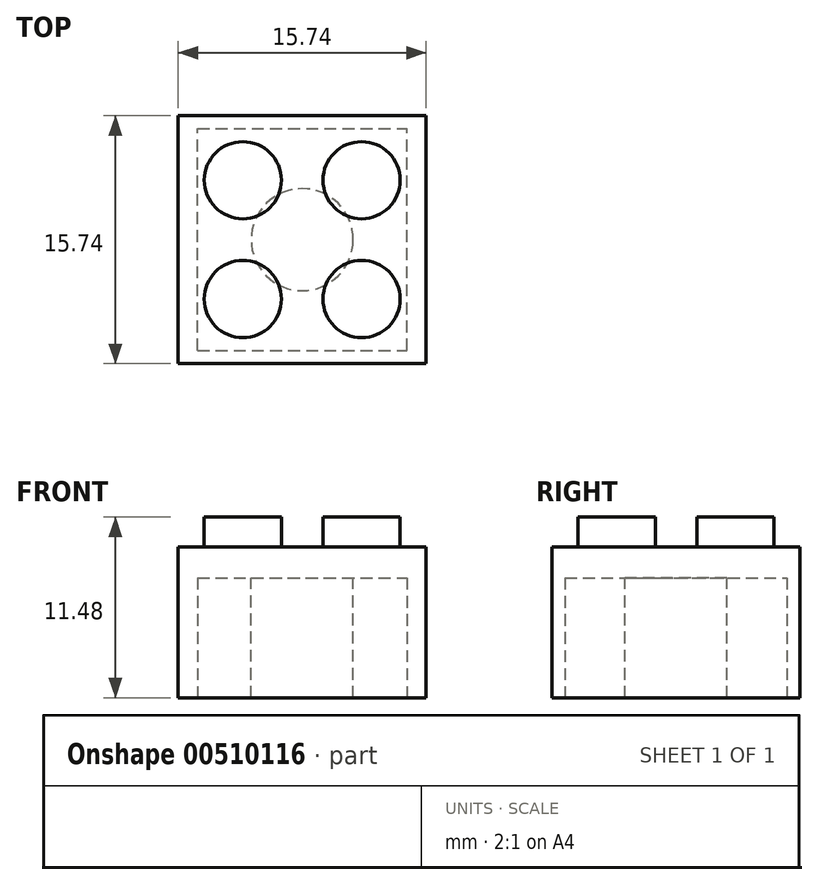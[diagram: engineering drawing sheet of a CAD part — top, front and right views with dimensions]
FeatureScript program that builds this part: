
annotation { "Feature Type Name" : "Feature", "Feature Type Description" : "" }
export const myFeature = defineFeature(function(context is Context, id is Id, definition is map)
    precondition{}
    {
        {
            var Q0;
            Q0=qCreatedBy(makeId("Top.planeOp"),FACE);
            var sketch = newSketch(context, id + "F0", { "sketchPlane" : qUnion([Q0])});
            skLineSegment(sketch, "E0.bottom", {"start": v(-7.87, 7.87) * mm, "end": v(7.87, 7.87) * mm});
            skLineSegment(sketch, "E0.top", {"start": v(-7.87, -7.87) * mm, "end": v(7.87, -7.87) * mm});
            skLineSegment(sketch, "E0.left", {"start": v(-7.87, 7.87) * mm, "end": v(-7.87, -7.87) * mm});
            skLineSegment(sketch, "E0.right", {"start": v(7.87, 7.87) * mm, "end": v(7.87, -7.87) * mm});
            skPoint(sketch, "E0.middle", {"position": v(0, 0) * mm});
            skSolve(sketch);
        }
        {
            var Q0;
            Q0=makeQuery(id+"F0.imprint","IMPRINT",FACE,{"disambiguationData":[TD([[makeQuery(id+"F0.imprint","IMPRINT",EDGE,{"derivedFrom":sQuery(id+"F0.wireOp",EDGE,"E0.bottom")}),-1.0]])]});
            extrude(context, id + "F1", {"entities" : qUnion([Q0]), "depth" : 9.58 * mm, "offsetDistance" : 25.4 * mm});
        }
        {
            var Q0;
            Q0=makeQuery(id+"F1.opExtrude","CAP_FACE",FACE,{"disambiguationData":[OSD([sQuery(id+"F0.wireOp",EDGE,"E0.bottom"),sQuery(id+"F0.wireOp",EDGE,"E0.top"),sQuery(id+"F0.wireOp",EDGE,"E0.left"),sQuery(id+"F0.wireOp",EDGE,"E0.right")])],"isStart":false});
            var sketch = newSketch(context, id + "F2", { "sketchPlane" : qUnion([Q0])});
            skCircle(sketch, "E1", {"center": v(-3.77, 3.77) * mm, "radius": 2.45 * mm});
            skSolve(sketch);
        }
        {
            var Q0;
            Q0=makeQuery(id+"F2.imprint","IMPRINT",FACE,{"disambiguationData":[TD([[makeQuery(id+"F2.imprint","IMPRINT",EDGE,{"derivedFrom":sQuery(id+"F2.wireOp",EDGE,"E1")}),-1.0]])]});
            var sketch = newSketch(context, id + "F3", { "sketchPlane" : qUnion([Q0])});
            skCircle(sketch, "E2", {"center": v(-3.77, -3.77) * mm, "radius": 2.45 * mm});
            skSolve(sketch);
        }
        {
            var Q0;
            Q0 = qSketchRegion(id + "F2", true);
            extrude(context, id + "F4", {"entities" : qUnion([Q0]), "operationType" : NewBodyOperationType.ADD, "depth" : 1.9 * mm, "offsetDistance" : 25.4 * mm});
        }
        {
            var Q0;
            Q0 = qSketchRegion(id + "F3", true);
            extrude(context, id + "F5", {"entities" : qUnion([Q0]), "operationType" : NewBodyOperationType.ADD, "depth" : 1.9 * mm, "offsetDistance" : 25.4 * mm});
        }
        {
            var Q0;
            Q0=makeQuery(id+"F1.opExtrude","CAP_FACE",FACE,{"disambiguationData":[OSD([sQuery(id+"F0.wireOp",EDGE,"E0.bottom"),sQuery(id+"F0.wireOp",EDGE,"E0.top"),sQuery(id+"F0.wireOp",EDGE,"E0.left"),sQuery(id+"F0.wireOp",EDGE,"E0.right")])],"isStart":false});
            var sketch = newSketch(context, id + "F6", { "sketchPlane" : qUnion([Q0])});
            skCircle(sketch, "E3", {"center": v(3.77, 3.77) * mm, "radius": 2.45 * mm});
            skCircle(sketch, "E4", {"center": v(3.77, -3.77) * mm, "radius": 2.45 * mm});
            skSolve(sketch);
        }
        {
            var Q0;
            Q0 = qSketchRegion(id + "F6", true);
            extrude(context, id + "F7", {"entities" : qUnion([Q0]), "operationType" : NewBodyOperationType.ADD, "depth" : 1.9 * mm, "offsetDistance" : 25.4 * mm});
        }
        {
            var Q0;
            Q0=makeQuery(id+"F1.opExtrude","CAP_FACE",FACE,{"disambiguationData":[OSD([sQuery(id+"F0.wireOp",EDGE,"E0.bottom"),sQuery(id+"F0.wireOp",EDGE,"E0.top"),sQuery(id+"F0.wireOp",EDGE,"E0.left"),sQuery(id+"F0.wireOp",EDGE,"E0.right")])],"isStart":true});
            var sketch = newSketch(context, id + "F8", { "sketchPlane" : qUnion([Q0])});
            skLineSegment(sketch, "E5.bottom", {"start": v(-6.64, 7.04) * mm, "end": v(6.64, 7.04) * mm});
            skLineSegment(sketch, "E5.top", {"start": v(-6.64, -7.04) * mm, "end": v(6.64, -7.04) * mm});
            skLineSegment(sketch, "E5.left", {"start": v(-6.64, 7.04) * mm, "end": v(-6.64, -7.04) * mm});
            skLineSegment(sketch, "E5.right", {"start": v(6.64, 7.04) * mm, "end": v(6.64, -7.04) * mm});
            skPoint(sketch, "E5.middle", {"position": v(0, 0) * mm});
            skSolve(sketch);
        }
        {
            var Q0;
            Q0=makeQuery(id+"F8.imprint","IMPRINT",FACE,{"disambiguationData":[TD([[makeQuery(id+"F8.imprint","IMPRINT",EDGE,{"derivedFrom":sQuery(id+"F8.wireOp",EDGE,"E5.bottom")}),-1.0]])]});
            extrude(context, id + "F9", {"entities" : qUnion([Q0]), "operationType" : NewBodyOperationType.REMOVE, "oppositeDirection" : true, "depth" : 7.62 * mm, "offsetDistance" : 25.4 * mm});
        }
        {
            var Q0;
            Q0=makeQuery(id+"F9.boolean.opBoolean","COPY",FACE,{"derivedFrom":makeQuery(id+"F9.opExtrude","CAP_FACE",FACE,{"disambiguationData":[OSD([sQuery(id+"F8.wireOp",EDGE,"E5.bottom"),sQuery(id+"F8.wireOp",EDGE,"E5.top"),sQuery(id+"F8.wireOp",EDGE,"E5.left"),sQuery(id+"F8.wireOp",EDGE,"E5.right")])],"isStart":false})});
            var sketch = newSketch(context, id + "F10", { "sketchPlane" : qUnion([Q0])});
            skCircle(sketch, "E6", {"center": v(0, 0) * mm, "radius": 3.24 * mm});
            skSolve(sketch);
        }
        {
            var Q0;
            Q0=makeQuery(id+"F10.imprint","IMPRINT",FACE,{"disambiguationData":[TD([[makeQuery(id+"F10.imprint","IMPRINT",EDGE,{"derivedFrom":sQuery(id+"F10.wireOp",EDGE,"E6")}),1.0]])]});
            extrude(context, id + "F11", {"entities" : qUnion([Q0]), "operationType" : NewBodyOperationType.ADD, "depth" : 7.62 * mm, "offsetDistance" : 25.4 * mm});
        }
    });
